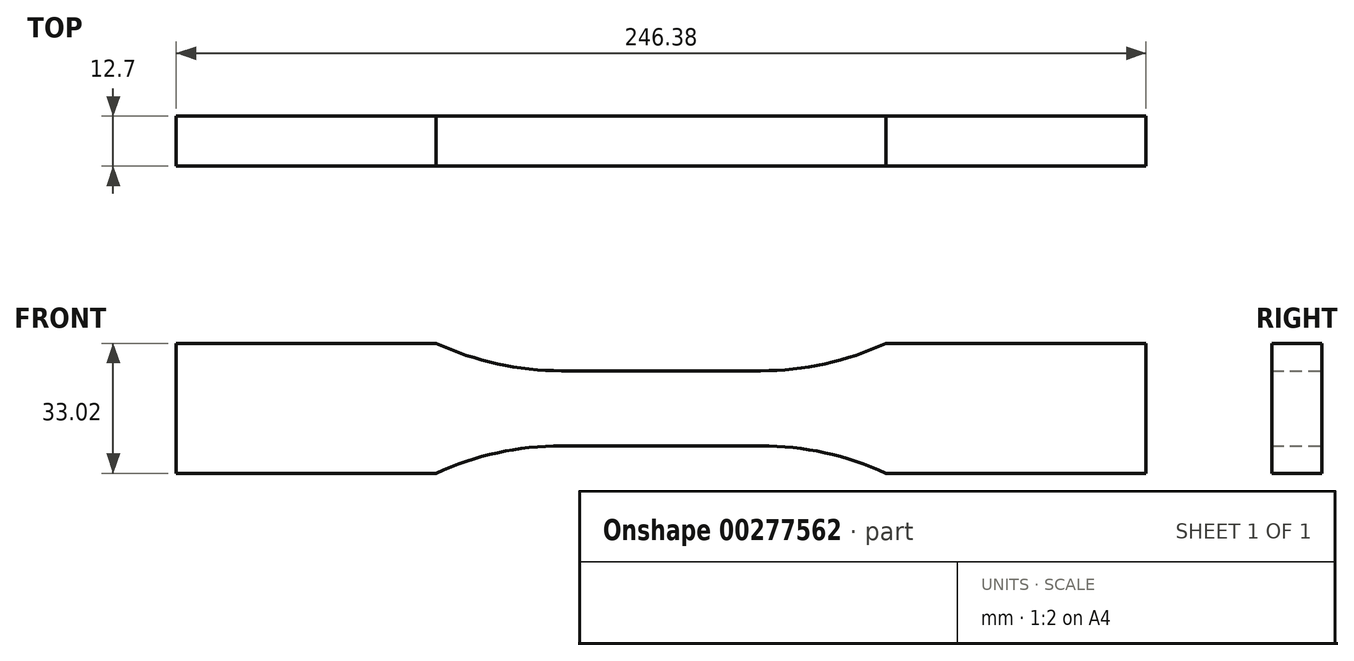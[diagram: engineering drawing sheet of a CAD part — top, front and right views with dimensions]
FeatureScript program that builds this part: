
annotation { "Feature Type Name" : "Feature", "Feature Type Description" : "" }
export const myFeature = defineFeature(function(context is Context, id is Id, definition is map)
    precondition{}
    {
        {
            var Q0;
            Q0=qCreatedBy(makeId("Front.planeOp"),FACE);
            var sketch = newSketch(context, id + "F0", { "sketchPlane" : qUnion([Q0])});
            skLineSegment(sketch, "E0", {"start": v(0, 9.52) * mm, "end": v(25.28, 9.52) * mm});
            skArc(sketch, "E1", {"start": v(25.28, 9.52) * mm, "mid": v(41.6, 11.3) * mm, "end": v(57.15, 16.5) * mm});
            skLineSegment(sketch, "E2", {"start": v(57.15, 16.51) * mm, "end": v(123.2, 16.51) * mm});
            skLineSegment(sketch, "E3", {"start": v(123.19, 16.51) * mm, "end": v(123.19, 0) * mm});
            skLineSegment(sketch, "E4.MirrorCS", {"start": v(0, -9.53) * mm, "end": v(25.28, -9.53) * mm});
            skLineSegment(sketch, "E5.MirrorCS", {"start": v(123.2, -16.51) * mm, "end": v(123.19, 0) * mm});
            skLineSegment(sketch, "E6.MirrorCS", {"start": v(57.15, -16.51) * mm, "end": v(123.2, -16.51) * mm});
            skArc(sketch, "E7.MirrorCS", {"start": v(25.28, -9.52) * mm, "mid": v(41.6, -11.3) * mm, "end": v(57.15, -16.5) * mm});
            skArc(sketch, "E8.MirrorCS", {"start": v(-25.28, -9.52) * mm, "mid": v(-41.6, -11.3) * mm, "end": v(-57.15, -16.5) * mm});
            skLineSegment(sketch, "E9.MirrorCS", {"start": v(-57.15, -16.51) * mm, "end": v(-123.2, -16.51) * mm});
            skArc(sketch, "E10.MirrorCS", {"start": v(-25.28, 9.52) * mm, "mid": v(-41.6, 11.3) * mm, "end": v(-57.15, 16.5) * mm});
            skLineSegment(sketch, "E11.MirrorCS", {"start": v(-57.15, 16.51) * mm, "end": v(-123.2, 16.51) * mm});
            skLineSegment(sketch, "E12.MirrorCS", {"start": v(-123.2, -16.51) * mm, "end": v(-123.2, 0) * mm});
            skLineSegment(sketch, "E13.MirrorCS", {"start": v(0, -9.53) * mm, "end": v(-25.28, -9.53) * mm});
            skLineSegment(sketch, "E14.MirrorCS", {"start": v(-123.2, 16.51) * mm, "end": v(-123.2, 0) * mm});
            skLineSegment(sketch, "E15.MirrorCS", {"start": v(0, 9.53) * mm, "end": v(-25.28, 9.53) * mm});
            skSolve(sketch);
        }
        {
            var Q0;
            Q0 = qSketchRegion(id + "F0", true);
            extrude(context, id + "F1", {"entities" : qUnion([Q0]), "depth" : 12.7 * mm});
        }
    });
